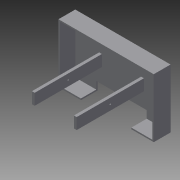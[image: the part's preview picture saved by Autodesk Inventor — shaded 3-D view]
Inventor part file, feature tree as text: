
AUTODESK INVENTOR PART (.ipt)
format: ipt  version: 2014 (Build 180170000, 170)  size: 143,360 bytes
history: native  units: in
note: dims shown in document units (in); Inventor stores cm internally (conversion verified against a paired STEP export)
features: extrude x8, sketch x7, projected_geometry x2, hole x1
ambient origin geometry x8: Origin, YZ Plane, XZ Plane, XY Plane, X Axis, Y Axis, Z Axis, Center Point
bodies: Solid1 (feature_tree)
feature tree (18):
  extrude  "Extrusion1"  Depth=21.0in
  sketch  "Sketch2"  dims[d2=6.0in d3=0.0in d6=3.0in d7=0.0in]
  extrude  "Extrusion2"  Depth=3.0in TaperAngle=0.0deg
  extrude  "Extrusion3"  Depth=3.0in TaperAngle=0.0deg
  sketch  "Sketch3"  dims[d8=2.0in d9=0.0in d10=3.0in d11=0.0in]
  extrude  "Extrusion4"  Depth=33.0in
  extrude  "Extrusion5"  Depth=5.5in TaperAngle=0.0deg
  extrude  "Extrusion6"  Depth=4.0in
  extrude  "Extrusion7"  Depth=12.0in
  hole  "Hole1"  [1 undecoded]
  extrude  "Extrusion8"  Depth=3.16in
  sketch  "Sketch1"  dims[d0=34.0in d1=21.0in]
  projected_geometry  "Projected Loop1"
  projected_geometry  "Projected Loop2"
  sketch  "Sketch4"  dims[d12=2.0in d13=0.0in d14=33.0in]
  sketch  "Sketch5"  dims[d15=20.0in d16=5.5in d17=0.0in]
  sketch  "Sketch6"  dims[d19=1.0in d20=4.0in]
  sketch  "Sketch7"  dims[d21=24.0in d22=0.0in d23=12.0in d24=0.5in d25=0.75in d26=0.375in d27=0.25in d28=0.5635in d29=1.0in d30=0.8108in d31=9.0in d32=3.16in d33=18.0in d34=24.0in d35=0.0in]
note: 1 required parameter value undecoded (feature->parameter linkage not recoverable at this tier; creation-order binding heuristic only, values carry confidence <= 0.55)
